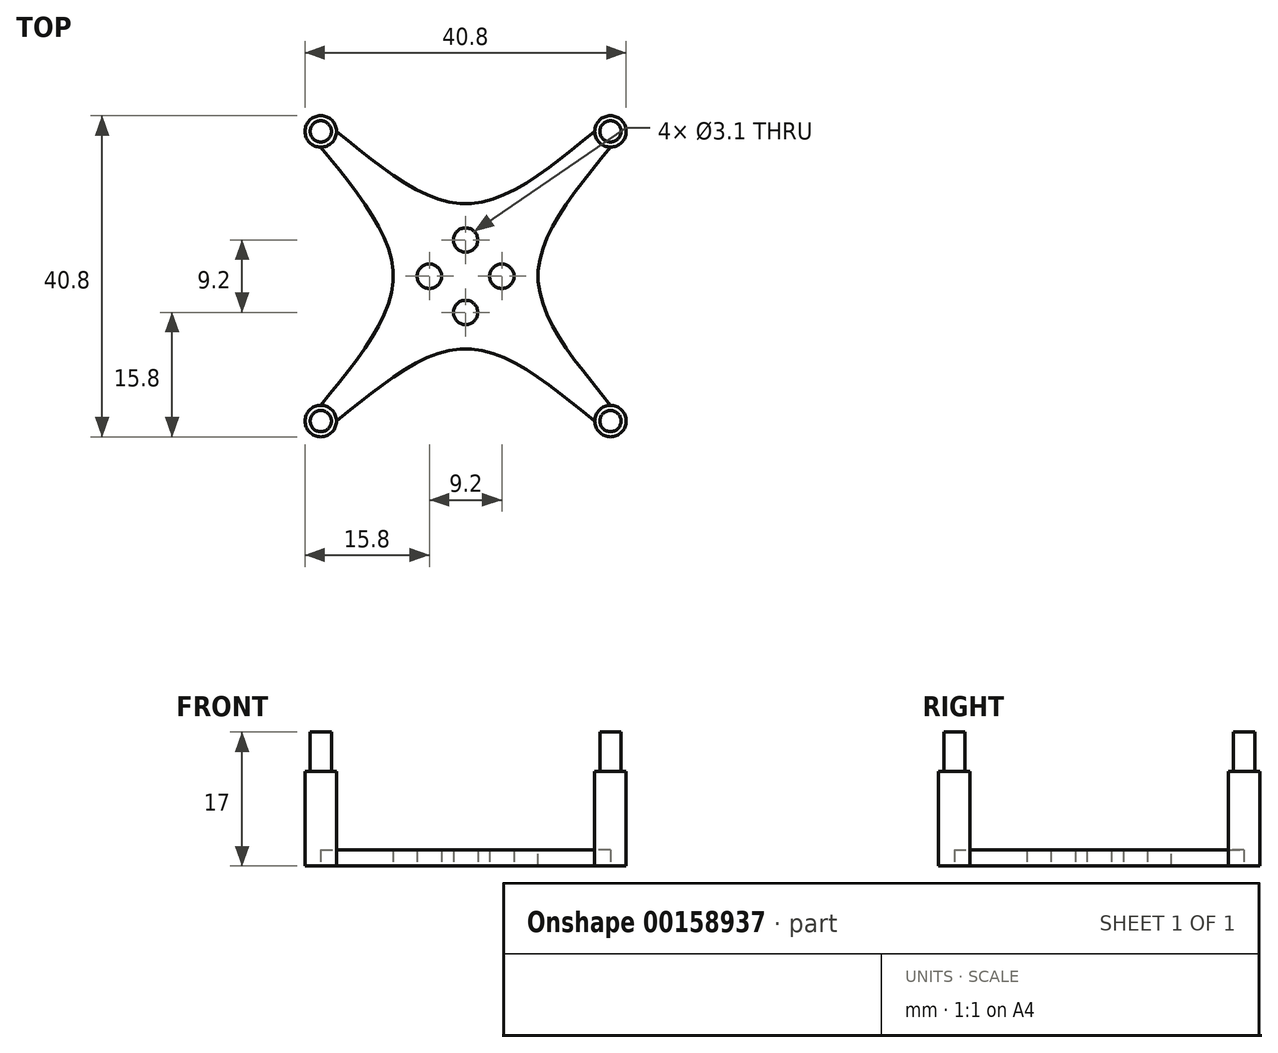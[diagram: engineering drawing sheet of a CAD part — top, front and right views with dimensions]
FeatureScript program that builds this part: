
annotation { "Feature Type Name" : "Feature", "Feature Type Description" : "" }
export const myFeature = defineFeature(function(context is Context, id is Id, definition is map)
    precondition{}
    {
        {
            var Q0;
            Q0=qCreatedBy(makeId("Top.planeOp"),FACE);
            var sketch = newSketch(context, id + "F0", { "sketchPlane" : qUnion([Q0])});
            skPoint(sketch, "E0.middle", {"position": v(0, 0) * mm});
            skCircle(sketch, "E1", {"center": v(18.4, 18.4) * mm, "radius": 2 * mm});
            skCircle(sketch, "E2", {"center": v(-18.4, 18.4) * mm, "radius": 2 * mm});
            skCircle(sketch, "E3", {"center": v(-18.4, -18.4) * mm, "radius": 2 * mm});
            skCircle(sketch, "E4", {"center": v(18.4, -18.4) * mm, "radius": 2 * mm});
            skFitSpline(sketch, "E5", {"points": [v(-18.4, 16.4) * mm, v(-9.2, 0) * mm, v(-18.4, -16.4) * mm], "startDerivative": vector(27.6, -34.2) * mm, "endDerivative": vector(-27.6, -34.2) * mm});
            skFitSpline(sketch, "E6", {"points": [v(-16.4, 18.4) * mm, v(0, 9.2) * mm, v(16.4, 18.4) * mm], "startDerivative": vector(34.2, -27.6) * mm, "endDerivative": vector(34.2, 27.6) * mm});
            skFitSpline(sketch, "E7", {"points": [v(18.4, 16.4) * mm, v(9.2, 0) * mm, v(18.4, -16.4) * mm], "startDerivative": vector(-27.6, -34.2) * mm, "endDerivative": vector(27.6, -34.2) * mm});
            skFitSpline(sketch, "E8", {"points": [v(-16.4, -18.4) * mm, v(0, -9.2) * mm, v(16.4, -18.4) * mm], "startDerivative": vector(34.2, 27.6) * mm, "endDerivative": vector(34.2, -27.6) * mm});
            skCircle(sketch, "E9", {"center": v(0, 4.6) * mm, "radius": 1.55 * mm});
            skCircle(sketch, "E10", {"center": v(-4.6, 0) * mm, "radius": 1.55 * mm});
            skCircle(sketch, "E11", {"center": v(4.6, 0) * mm, "radius": 1.55 * mm});
            skCircle(sketch, "E12", {"center": v(0, -4.6) * mm, "radius": 1.55 * mm});
            skSolve(sketch);
        }
        {
            var Q0;
            {var subQ0=sQuery(id+"F0.wireOp",EDGE,"E1");var subQ1=makeQuery(id+"F0.imprint","INTERSECT",VERTEX,{"derivedFrom":[subQ0,sQuery(id+"F0.wireOp",EDGE,"E6")]});Q0=makeQuery(id+"F0.imprint","IMPRINT",FACE,{"disambiguationData":[TD([[makeQuery(id+"F0.imprint","IMPRINT",EDGE,{"disambiguationData":[TD([[subQ1,-1.0]])],"derivedFrom":subQ0}),1.0]])]});}
            var Q1;
            {var subQ0=sQuery(id+"F0.wireOp",EDGE,"E3");var subQ1=makeQuery(id+"F0.imprint","INTERSECT",VERTEX,{"derivedFrom":[subQ0,sQuery(id+"F0.wireOp",EDGE,"E5")]});Q1=makeQuery(id+"F0.imprint","IMPRINT",FACE,{"disambiguationData":[TD([[makeQuery(id+"F0.imprint","IMPRINT",EDGE,{"disambiguationData":[TD([[subQ1,1.0]])],"derivedFrom":subQ0}),1.0]])]});}
            var Q2;
            {var subQ0=sQuery(id+"F0.wireOp",EDGE,"E4");var subQ1=makeQuery(id+"F0.imprint","INTERSECT",VERTEX,{"derivedFrom":[subQ0,sQuery(id+"F0.wireOp",EDGE,"E7")]});Q2=makeQuery(id+"F0.imprint","IMPRINT",FACE,{"disambiguationData":[TD([[makeQuery(id+"F0.imprint","IMPRINT",EDGE,{"disambiguationData":[TD([[subQ1,-1.0]])],"derivedFrom":subQ0}),1.0]])]});}
            var Q3;
            {var subQ0=sQuery(id+"F0.wireOp",EDGE,"E2");var subQ1=makeQuery(id+"F0.imprint","INTERSECT",VERTEX,{"derivedFrom":[subQ0,sQuery(id+"F0.wireOp",EDGE,"E5")]});Q3=makeQuery(id+"F0.imprint","IMPRINT",FACE,{"disambiguationData":[TD([[makeQuery(id+"F0.imprint","IMPRINT",EDGE,{"disambiguationData":[TD([[subQ1,1.0]])],"derivedFrom":subQ0}),1.0]])]});}
            extrude(context, id + "F1", {"entities" : qUnion([Q0, Q1, Q2, Q3]), "depth" : 12 * mm});
        }
        {
            var Q0;
            {var subQ0=sQuery(id+"F0.wireOp",EDGE,"E5");Q0=makeQuery(id+"F0.imprint","IMPRINT",FACE,{"disambiguationData":[TD([[makeQuery(id+"F0.imprint","IMPRINT",EDGE,{"derivedFrom":subQ0}),1.0]])]});}
            extrude(context, id + "F2", {"entities" : qUnion([Q0]), "depth" : 2 * mm});
        }
        {
            var Q0;
            Q0=makeQuery(id+"F1.opExtrude","CAP_FACE",FACE,{"disambiguationData":[OSD([sQuery(id+"F0.wireOp",EDGE,"E1")])],"isStart":false});
            var sketch = newSketch(context, id + "F3", { "sketchPlane" : qUnion([Q0])});
            skCircle(sketch, "E13", {"center": v(18.4, 18.4) * mm, "radius": 1.35 * mm});
            skSolve(sketch);
        }
        {
            var Q0;
            Q0=makeQuery(id+"F3.imprint","IMPRINT",FACE,{"disambiguationData":[TD([[makeQuery(id+"F3.imprint","IMPRINT",EDGE,{"derivedFrom":sQuery(id+"F3.wireOp",EDGE,"E13")}),1.0]])]});
            extrude(context, id + "F4", {"entities" : qUnion([Q0]), "operationType" : NewBodyOperationType.ADD, "depth" : 5 * mm});
        }
        {
            var Q0;
            Q0=makeQuery(id+"F1.opExtrude","CAP_FACE",FACE,{"disambiguationData":[OSD([sQuery(id+"F0.wireOp",EDGE,"E4")])],"isStart":false});
            var sketch = newSketch(context, id + "F5", { "sketchPlane" : qUnion([Q0])});
            skCircle(sketch, "E14", {"center": v(18.4, -18.4) * mm, "radius": 1.35 * mm});
            skSolve(sketch);
        }
        {
            var Q0;
            Q0=makeQuery(id+"F5.imprint","IMPRINT",FACE,{"disambiguationData":[TD([[makeQuery(id+"F5.imprint","IMPRINT",EDGE,{"derivedFrom":sQuery(id+"F5.wireOp",EDGE,"E14")}),1.0]])]});
            extrude(context, id + "F6", {"entities" : qUnion([Q0]), "operationType" : NewBodyOperationType.ADD, "depth" : 5 * mm});
        }
        {
            var Q0;
            Q0=makeQuery(id+"F1.opExtrude","CAP_FACE",FACE,{"disambiguationData":[OSD([sQuery(id+"F0.wireOp",EDGE,"E3")])],"isStart":false});
            var sketch = newSketch(context, id + "F7", { "sketchPlane" : qUnion([Q0])});
            skCircle(sketch, "E15", {"center": v(-18.4, -18.4) * mm, "radius": 1.35 * mm});
            skSolve(sketch);
        }
        {
            var Q0;
            Q0=makeQuery(id+"F7.imprint","IMPRINT",FACE,{"disambiguationData":[TD([[makeQuery(id+"F7.imprint","IMPRINT",EDGE,{"derivedFrom":sQuery(id+"F7.wireOp",EDGE,"E15")}),1.0]])]});
            extrude(context, id + "F8", {"entities" : qUnion([Q0]), "operationType" : NewBodyOperationType.ADD, "depth" : 5 * mm});
        }
        {
            var Q0;
            Q0=makeQuery(id+"F1.opExtrude","CAP_FACE",FACE,{"disambiguationData":[OSD([sQuery(id+"F0.wireOp",EDGE,"E2")])],"isStart":false});
            var sketch = newSketch(context, id + "F9", { "sketchPlane" : qUnion([Q0])});
            skCircle(sketch, "E16", {"center": v(-18.4, 18.4) * mm, "radius": 1.35 * mm});
            skSolve(sketch);
        }
        {
            var Q0;
            Q0=makeQuery(id+"F9.imprint","IMPRINT",FACE,{"disambiguationData":[TD([[makeQuery(id+"F9.imprint","IMPRINT",EDGE,{"derivedFrom":sQuery(id+"F9.wireOp",EDGE,"E16")}),1.0]])]});
            extrude(context, id + "F10", {"entities" : qUnion([Q0]), "operationType" : NewBodyOperationType.ADD, "depth" : 5 * mm});
        }
    });
